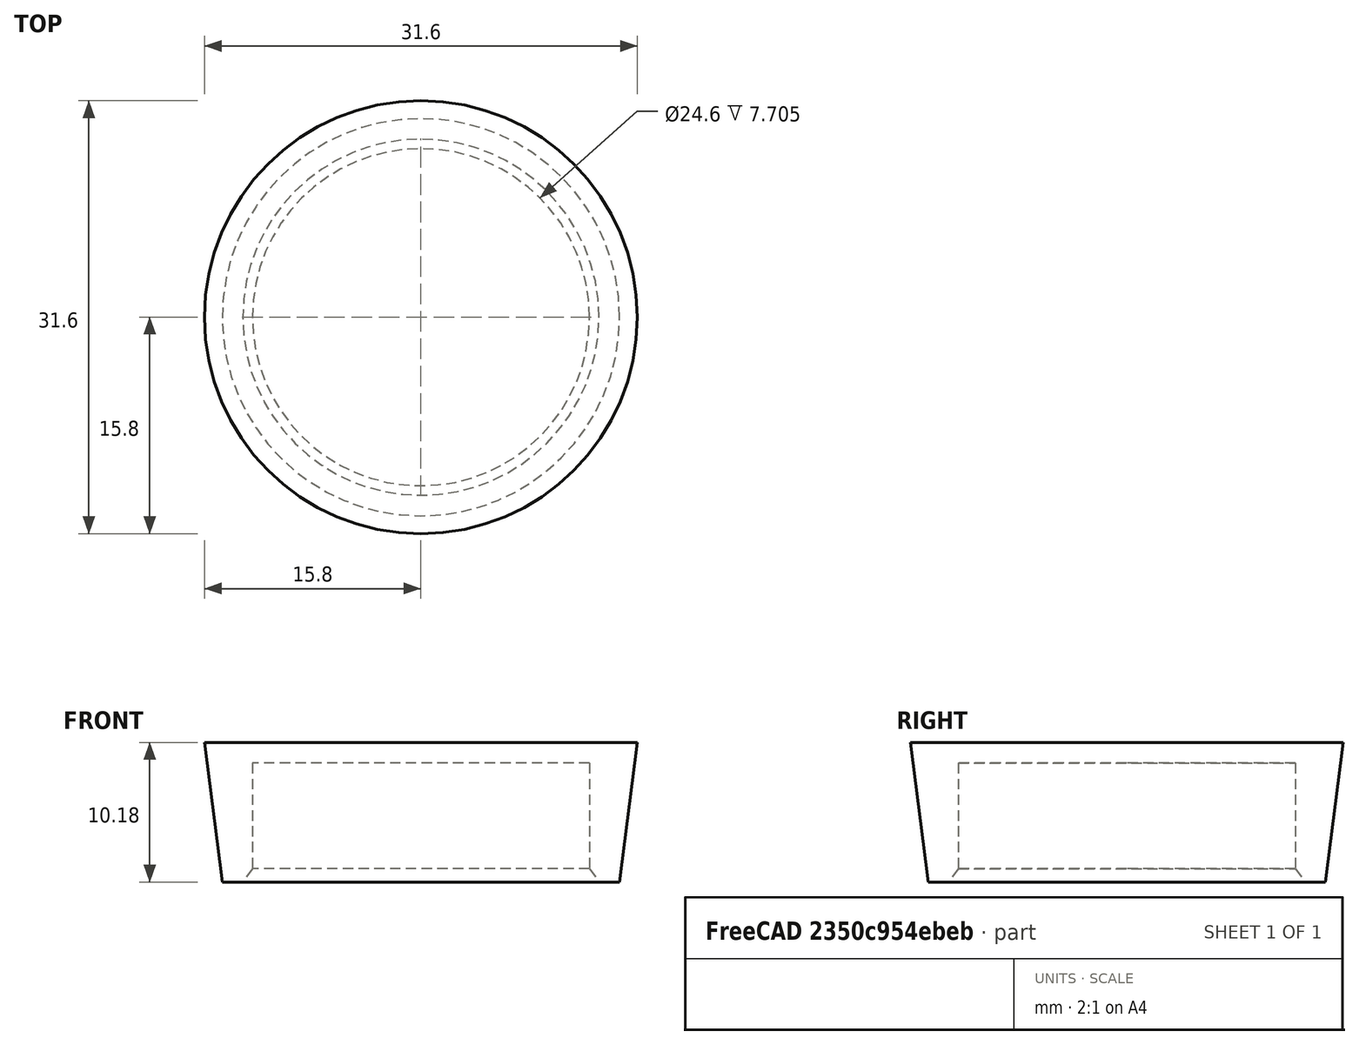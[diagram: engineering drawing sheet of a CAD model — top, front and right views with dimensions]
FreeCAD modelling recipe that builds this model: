
FCSTD DOCUMENT  (FreeCAD 1.0R39285 (Git))
Label: Крышка
License: All rights reserved
LicenseURL: https://en.wikipedia.org/wiki/All_rights_reserved
objects: Sketcher::SketchObject×1, PartDesign::Revolution×1, PartDesign::Body×1
note: 6 computed .brp shape members not serialized (recipe doc carries the construction recipe); baked Part::Feature solids carry a one-line shape summary decoded from their .brp

FEATURE [Sketcher::SketchObject] Sketch
  ArcFitTolerance = 1e-06
  AttachmentSupport = -> [XZ_Plane]
  FullyConstrained = false
  MakeInternals = false
  MapMode = 5
  Placement = pos=(0,0,0) rot=(1,0,0;1.5708rad)
  sketch-geometry (7):
    g0: LineSegment StartX=12.3 StartY=0.972585 StartZ=0 EndX=13 EndY=1e-16 EndZ=0
    g1: LineSegment StartX=13 StartY=1e-16 StartZ=0 EndX=14.5 EndY=0 EndZ=0
    g2: LineSegment StartX=14.5 StartY=0 StartZ=0 EndX=15.8 EndY=10.1772 EndZ=0
    g3: LineSegment StartX=15.8 StartY=10.1772 StartZ=0 EndX=0 EndY=10.1772 EndZ=0
    g4: LineSegment StartX=0 StartY=10.1772 StartZ=0 EndX=0 EndY=8.67725 EndZ=0
    g5: LineSegment StartX=0 StartY=8.67725 StartZ=0 EndX=12.3 EndY=8.67725 EndZ=0
    g6: LineSegment StartX=12.3 StartY=8.67725 StartZ=0 EndX=12.3 EndY=0.972585 EndZ=0
  constraints (18):
    c: PointOnObject(g0,g-1)
    c: DistanceX(g-1,g0) = 13
    c: DistanceX(g-1,g0) = 12.3
    c: Coincident(g0,g1)
    c: PointOnObject(g1,g-1)
    c: Coincident(g1,g2)
    c: Coincident(g2,g3)
    c: Horizontal(g3)
    c: Coincident(g3,g4)
    c: Vertical(g4)
    c: Coincident(g4,g5)
    c: Horizontal(g5)
    c: Coincident(g5,g6)
    c: Coincident(g6,g0)
    c: Vertical(g6)
    c: Distance(g2,g6) = 2.2
    c: Distance(g2,g6) = 3.5
    c: DistanceY(g4,g4) = 1.5
FEATURE [PartDesign::Revolution] Revolution
  Angle = 360
  Angle2 = 60
  Axis = (0,2e-16,1)
  Base = (0,0,0)
  Placement = pos=(0,0,0) rot=(1,0,0;1.5708rad)
  Profile = -> Sketch
  ReferenceAxis = -> Sketch [V_Axis]
  Refine = true
  Reversed = true
  Suppressed = false
  Type = 0
FEATURE [PartDesign::Body] Body  label="Тело"
  AllowCompound = false
  Group = -> [Sketch,Revolution]
  Origin = -> Origin
  Tip = -> Revolution
